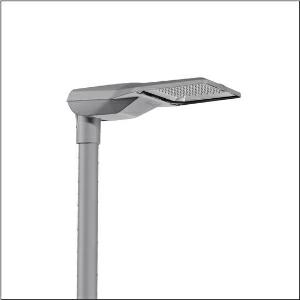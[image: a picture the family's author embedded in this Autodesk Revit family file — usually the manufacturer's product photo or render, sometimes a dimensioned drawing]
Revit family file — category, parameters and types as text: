
# Revit family: streetlight_sl_21_iq_midi___stw1_0a_5xe3e31d08mb_516a
name_source: partatom
category: Lighting Fixtures
units: mm (PartAtom-declared; Revit-internal decimal feet)

## family parameters
Cut with Voids When Loaded = No
Host = Face
Light Source = No
Part Type = Normal
Room Calculation Point = No
Round Connector Dimension = Use Diameter
Shared = No

## types (1)
- --- (1 x LED, 19500 lm, 146.7 W, 3000K)
    Apparent Load = 147 VA
    CIE Flux Codes = 38 75 98 100 100
    Color Rendering = 70
    Color Temperature = 3000K
    Default Elevation = 1800 mm
    Description = Streetlight SL 21 iQ midi, mast luminaire, primary light control with lens, of PMMA, primary optical cover: cover, of toughened safety glass, transparent, light distribution: STW1.0a, light emission: direct distribution, primary light characteristic: asymmetric, installation type: post-top, side-entry, LED, High Power LED, rated luminous flux: 19.500lm, luminous efficacy: 133lm/W, light colour: 730, colour temperature: 3000K, control: Auto-Match, Temp-Guard, Lumen-Switch, Night-Set, Smart-Wire, Light-Fading, Desk-Remote (wireless, voltage-free reading and setting of iQ features in the workshop via application-optimized NFC function/RFID function), optimised constant luminous flux control (CLO 2.0), presetting dimming linear, mains connection: 230..240V, AC, 50/60Hz, start of lifetime: 147W, end of service life: 161W, reduction: 62W, luminaire housing, of diecast aluminium, powder-coated, Siteco® metallic grey (DB 702S), corrosivity category C5 mid according to DIN EN ISO 12944, please order mast flange separately, inclination adjustable: 0°, 5°, 10°, 15°, sealing non-destructively replaceable, multi-level sealing system, length: 644mm, width: 335mm, height: 110mm, mast flange for spigot size: 42mm (side-entry): 5XC10008XM4, 60/48mm (side-entry/post-top): 5XC10108XM2, 76/60mm (side-entry/post-top): 5XC10108XM1, protection rating (complete): IP66, insulation class (complete): insulation class II (safety insulation), certification: CE, ENEC, ENEC+, VDE, impact resistance: IK09, permissible operating ambient temperature for outdoor applications: -40..+50°C, standard-compliant lighting for roads and squares, packaging unit: 1 piece

Light Distribution: STW1.0a
    Height = 111 mm
    Lamp = 1 x LED
    Lamp Light Flux = 19500 lm
    Lamp Power = 146.7 W
    Lamp count = 1
    Length = 644 mm
    Luminous efficacy = 133 lm/W
    Manufacturer = Siteco
    ModVariant = No
    Model = 5XE3E31D08MB
    Number of Poles = 1
    OnlyDefault = Yes
    Power Factor = 1
    Product Name = Streetlight SL 21 iQ midi | STW1.0a
    Product group = mast luminaire | pylon top
    ProductGroupID = 6100
    Protection Class = Protection class II
    Protection Degree = IP 66
    RLX_Detail_Level = 1
    RLX_Emergency_Light_Flux = 0 lm
    RLX_Emergency_Type = 0
    RLX_Emergency_Type_DB = No
    RlxData = <blob elided: 90341 chars, md5=d3df87d8>
    Socket = socket
    Standby Power = 0 W
    System Light Flux = 19499 lm
    System Power = 147 W
    Type Comments = factory setting: luminous flux: 100 % | dim-lin: 254 | 753 mA
    Type Image = l_1004298.jpg
    URL = http://relux.com
    VarID = @adj_121863
    Voltage = 0 V
    Weight = 0.00 kg
    Width = 336 mm

## geometry (parser evidence)
native form markers: Blend x4, Sweep x10
no freeform markers — native parametric forms only
